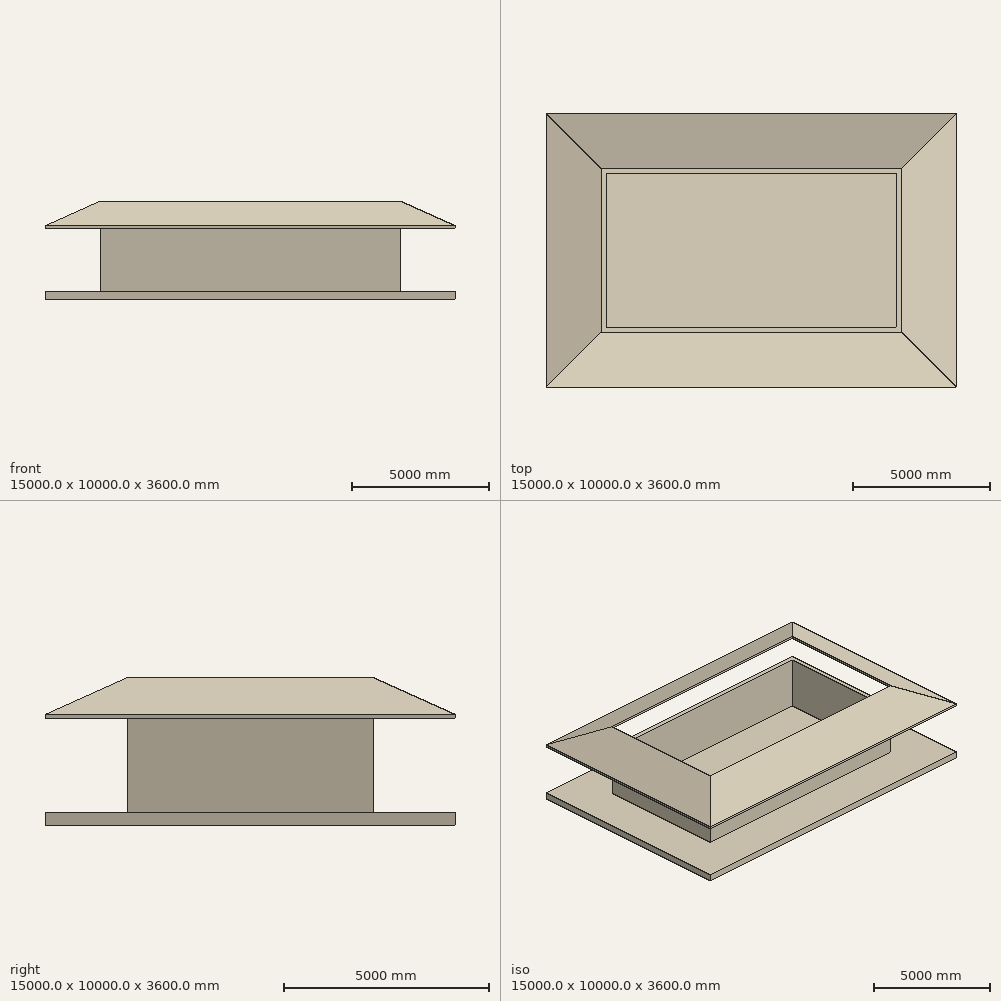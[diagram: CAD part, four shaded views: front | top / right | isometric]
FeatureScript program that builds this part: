
annotation { "Feature Type Name" : "Feature", "Feature Type Description" : "" }
export const myFeature = defineFeature(function(context is Context, id is Id, definition is map)
    precondition{}
    {
        {
            var Q0;
            Q0=qCreatedBy(makeId("Top.planeOp"),FACE);
            var sketch = newSketch(context, id + "F0", { "sketchPlane" : qUnion([Q0])});
            skLineSegment(sketch, "E0.bottom", {"start": v(-15000, 10000) * mm, "end": v(0, 10000) * mm});
            skLineSegment(sketch, "E0.top", {"start": v(-15000, 0) * mm, "end": v(0, 0) * mm});
            skLineSegment(sketch, "E0.left", {"start": v(-15000, 10000) * mm, "end": v(-15000, 0) * mm});
            skLineSegment(sketch, "E0.right", {"start": v(0, 10000) * mm, "end": v(0, 0) * mm});
            skSolve(sketch);
        }
        {
            var Q0;
            Q0=makeQuery(id+"F0.imprint","IMPRINT",FACE,{"disambiguationData":[TD([[makeQuery(id+"F0.imprint","IMPRINT",EDGE,{"derivedFrom":sQuery(id+"F0.wireOp",EDGE,"E0.bottom")}),-1.0]])]});
            extrude(context, id + "F1", {"entities" : qUnion([Q0]), "depth" : 300 * mm, "offsetDistance" : 25 * mm});
        }
        {
            var Q0;
            Q0=makeQuery(id+"F1.opExtrude","CAP_FACE",FACE,{"disambiguationData":[OSD([sQuery(id+"F0.wireOp",EDGE,"E0.bottom"),sQuery(id+"F0.wireOp",EDGE,"E0.top"),sQuery(id+"F0.wireOp",EDGE,"E0.left"),sQuery(id+"F0.wireOp",EDGE,"E0.right")])],"isStart":false});
            var sketch = newSketch(context, id + "F2", { "sketchPlane" : qUnion([Q0])});
            skLineSegment(sketch, "E1.bottom", {"start": v(-13000, 8000) * mm, "end": v(-2000, 8000) * mm});
            skLineSegment(sketch, "E1.top", {"start": v(-13000, 2000) * mm, "end": v(-2000, 2000) * mm});
            skLineSegment(sketch, "E1.left", {"start": v(-13000, 8000) * mm, "end": v(-13000, 2000) * mm});
            skLineSegment(sketch, "E1.right", {"start": v(-2000, 8000) * mm, "end": v(-2000, 2000) * mm});
            skLineSegment(sketch, "E2.bottom", {"start": v(-12800, 7800) * mm, "end": v(-2200, 7800) * mm});
            skLineSegment(sketch, "E2.top", {"start": v(-12800, 2200) * mm, "end": v(-2200, 2200) * mm});
            skLineSegment(sketch, "E2.left", {"start": v(-12800, 7800) * mm, "end": v(-12800, 2200) * mm});
            skLineSegment(sketch, "E2.right", {"start": v(-2200, 7800) * mm, "end": v(-2200, 2200) * mm});
            skSolve(sketch);
        }
        {
            var Q0;
            Q0 = qSketchRegion(id + "F2", true);
            extrude(context, id + "F3", {"entities" : qUnion([Q0]), "operationType" : NewBodyOperationType.ADD, "depth" : 2300 * mm, "offsetDistance" : 25 * mm});
        }
        {
            var Q0;
            Q0=makeQuery(id+"F3.opExtrude","CAP_FACE",FACE,{"disambiguationData":[OSD([sQuery(id+"F2.wireOp",EDGE,"E1.bottom"),sQuery(id+"F2.wireOp",EDGE,"E1.top"),sQuery(id+"F2.wireOp",EDGE,"E1.left"),sQuery(id+"F2.wireOp",EDGE,"E1.right"),sQuery(id+"F2.wireOp",EDGE,"E2.bottom"),sQuery(id+"F2.wireOp",EDGE,"E2.top"),sQuery(id+"F2.wireOp",EDGE,"E2.left"),sQuery(id+"F2.wireOp",EDGE,"E2.right")])],"isStart":false});
            var sketch = newSketch(context, id + "F4", { "sketchPlane" : qUnion([Q0])});
            skLineSegment(sketch, "E3.bottom", {"start": v(-15000, 10000) * mm, "end": v(0, 10000) * mm});
            skLineSegment(sketch, "E3.top", {"start": v(-15000, 0) * mm, "end": v(0, 0) * mm});
            skLineSegment(sketch, "E3.left", {"start": v(-15000, 10000) * mm, "end": v(-15000, 0) * mm});
            skLineSegment(sketch, "E3.right", {"start": v(0, 10000) * mm, "end": v(0, 0) * mm});
            skLineSegment(sketch, "E4.bottom", {"start": v(-13000, 2000) * mm, "end": v(-2000, 2000) * mm});
            skLineSegment(sketch, "E4.top", {"start": v(-13000, 8000) * mm, "end": v(-2000, 8000) * mm});
            skLineSegment(sketch, "E4.left", {"start": v(-13000, 2000) * mm, "end": v(-13000, 8000) * mm});
            skLineSegment(sketch, "E4.right", {"start": v(-2000, 2000) * mm, "end": v(-2000, 8000) * mm});
            skSolve(sketch);
        }
        {
            var Q0;
            Q0=makeQuery(id+"F4.imprint","IMPRINT",FACE,{"disambiguationData":[TD([[makeQuery(id+"F4.imprint","IMPRINT",EDGE,{"derivedFrom":sQuery(id+"F4.wireOp",EDGE,"E3.bottom")}),-1.0]])]});
            var Q1;
            Q1=makeQuery(id+"F4.imprint","IMPRINT",FACE,{"disambiguationData":[TD([[makeQuery(id+"F4.imprint","IMPRINT",EDGE,{"derivedFrom":makeQuery(id+"F3.opExtrude","CAP_EDGE",EDGE,{"disambiguationData":[OSD([sQuery(id+"F2.wireOp",EDGE,"E1.bottom")])],"isStart":false})}),-1.0]])]});
            extrude(context, id + "F5", {"entities" : qUnion([Q0, Q1]), "operationType" : NewBodyOperationType.ADD, "depth" : 1000 * mm, "offsetDistance" : 25 * mm});
        }
        {
            var Q0;
            Q0=makeQuery(id+"F5.opExtrude","CAP_EDGE",EDGE,{"disambiguationData":[OSD([sQuery(id+"F4.wireOp",EDGE,"E3.top")])],"isStart":false});
            var Q1;
            Q1=makeQuery(id+"F5.opExtrude","CAP_EDGE",EDGE,{"disambiguationData":[OSD([sQuery(id+"F4.wireOp",EDGE,"E3.bottom")])],"isStart":false});
            var Q2;
            Q2=makeQuery(id+"F5.opExtrude","CAP_EDGE",EDGE,{"disambiguationData":[OSD([sQuery(id+"F4.wireOp",EDGE,"E3.left")])],"isStart":false});
            var Q3;
            Q3=makeQuery(id+"F5.opExtrude","CAP_EDGE",EDGE,{"disambiguationData":[OSD([sQuery(id+"F4.wireOp",EDGE,"E3.right")])],"isStart":false});
            chamfer(context, id + "F6", {"entities" : qUnion([Q0, Q1, Q2, Q3]), "chamferType" : ChamferType.TWO_OFFSETS, "width1" : 2000 * mm, "oppositeDirection" : false, "width2" : 900 * mm, "tangentPropagation" : true});
        }
        {
            var Q0;
            Q0=makeQuery(id+"F5.opExtrude","CAP_EDGE",EDGE,{"disambiguationData":[OSD([sQuery(id+"F4.wireOp",EDGE,"E4.bottom")])],"isStart":true});
            var Q1;
            Q1=makeQuery(id+"F5.opExtrude","CAP_EDGE",EDGE,{"disambiguationData":[OSD([sQuery(id+"F4.wireOp",EDGE,"E4.top")])],"isStart":true});
            var Q2;
            Q2=makeQuery(id+"F5.opExtrude","CAP_EDGE",EDGE,{"disambiguationData":[OSD([sQuery(id+"F4.wireOp",EDGE,"E4.left")])],"isStart":true});
            var Q3;
            Q3=makeQuery(id+"F5.opExtrude","CAP_EDGE",EDGE,{"disambiguationData":[OSD([sQuery(id+"F4.wireOp",EDGE,"E4.right")])],"isStart":true});
            chamfer(context, id + "F7", {"entities" : qUnion([Q0, Q1, Q2, Q3]), "chamferType" : ChamferType.TWO_OFFSETS, "width1" : 2000 * mm, "oppositeDirection" : false, "width2" : 900 * mm, "tangentPropagation" : true});
        }
    });
